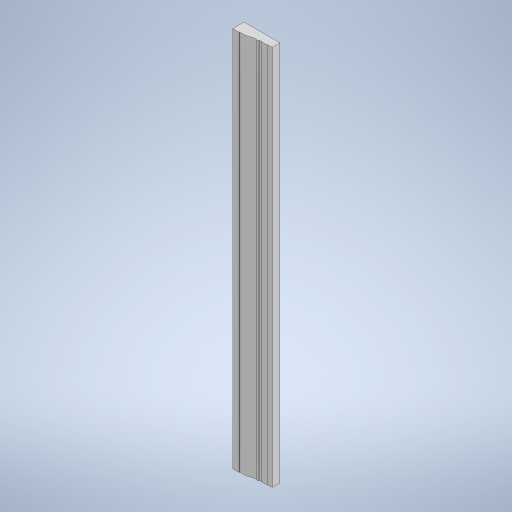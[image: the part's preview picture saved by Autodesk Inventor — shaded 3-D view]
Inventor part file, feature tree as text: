
AUTODESK INVENTOR PART (.ipt)
format: ipt  version: 2023 (Build 270158000, 158)  size: 921,088 bytes
history: native  units: mm
features: extrude x1, sketch x1, other x1
ambient origin geometry x8: Origin, YZ Plane, XZ Plane, XY Plane, X Axis, Y Axis, Z Axis, Center Point
bodies: Solid1 (feature_tree)
feature tree (3):
  extrude  "Extrusion1"  Depth=18.0mm
  sketch  "Sketch1"  dims[d25=609.6mm d26=0.0mm d100=66.085735mm d113=5.0mm d119=30.175621mm d121=20.965007mm d140=18.0mm]
  other  "Image2"
